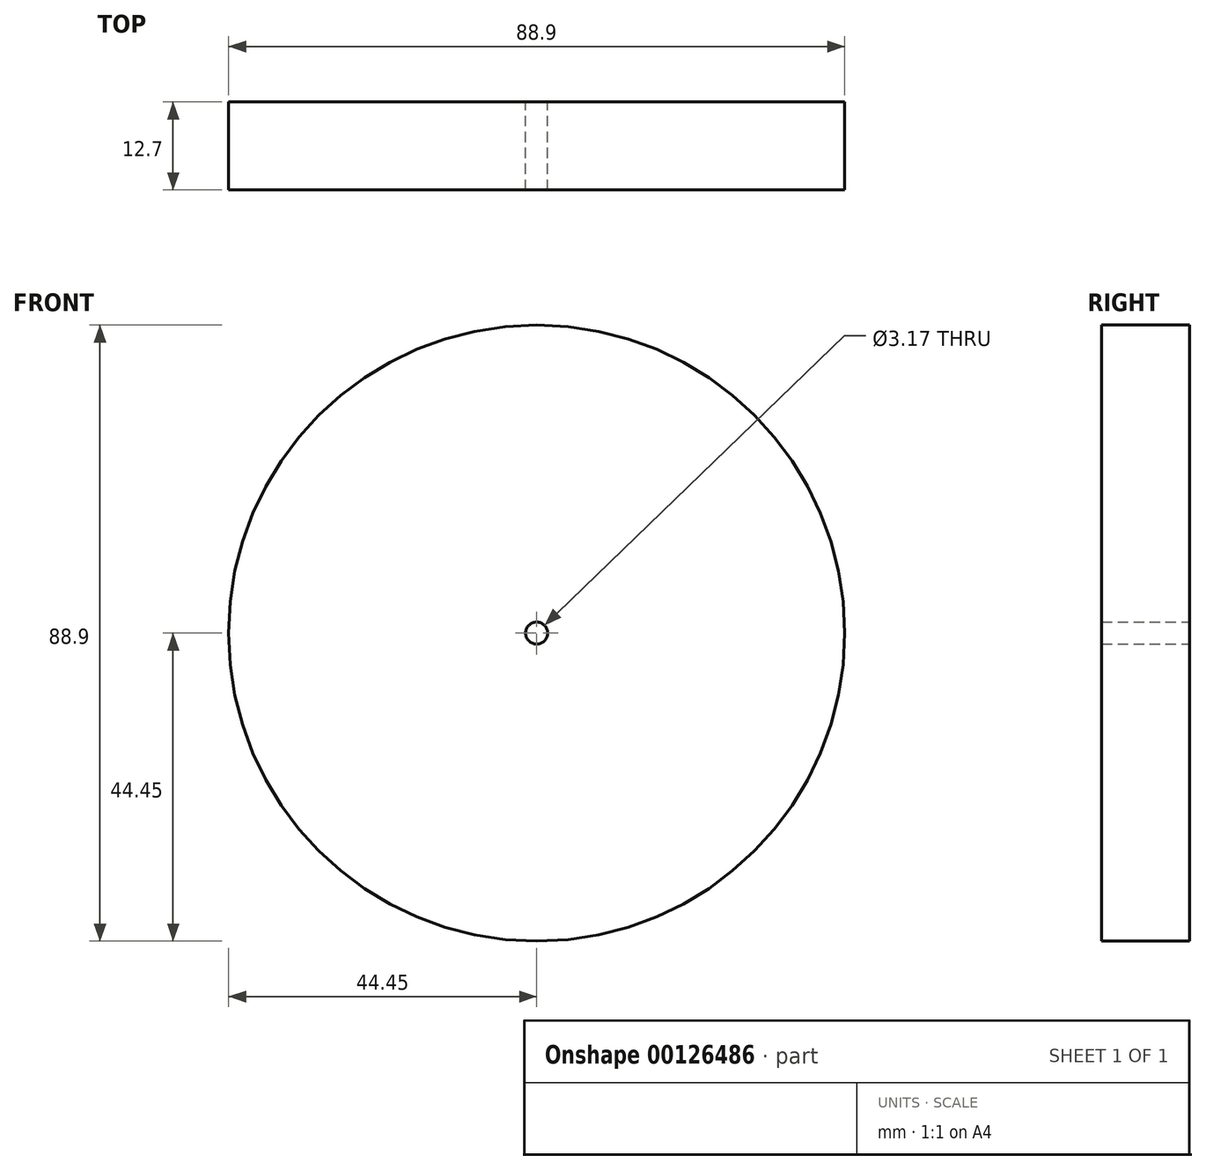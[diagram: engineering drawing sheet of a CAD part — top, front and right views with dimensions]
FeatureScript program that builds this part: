
annotation { "Feature Type Name" : "Feature", "Feature Type Description" : "" }
export const myFeature = defineFeature(function(context is Context, id is Id, definition is map)
    precondition{}
    {
        {
            var Q0;
            Q0=qCreatedBy(makeId("Front.planeOp"),FACE);
            var sketch = newSketch(context, id + "F0", { "sketchPlane" : qUnion([Q0])});
            skCircle(sketch, "E0", {"center": v(0, 0) * mm, "radius": 44.45 * mm});
            skCircle(sketch, "E1", {"center": v(0, 0) * mm, "radius": 1.59 * mm});
            skSolve(sketch);
        }
        {
            var Q0;
            Q0=makeQuery(id+"F0.imprint","IMPRINT",FACE,{"disambiguationData":[TD([[makeQuery(id+"F0.imprint","IMPRINT",EDGE,{"derivedFrom":sQuery(id+"F0.wireOp",EDGE,"E0")}),1.0]])]});
            extrude(context, id + "F1", {"entities" : qUnion([Q0]), "depth" : 12.7 * mm});
        }
    });
